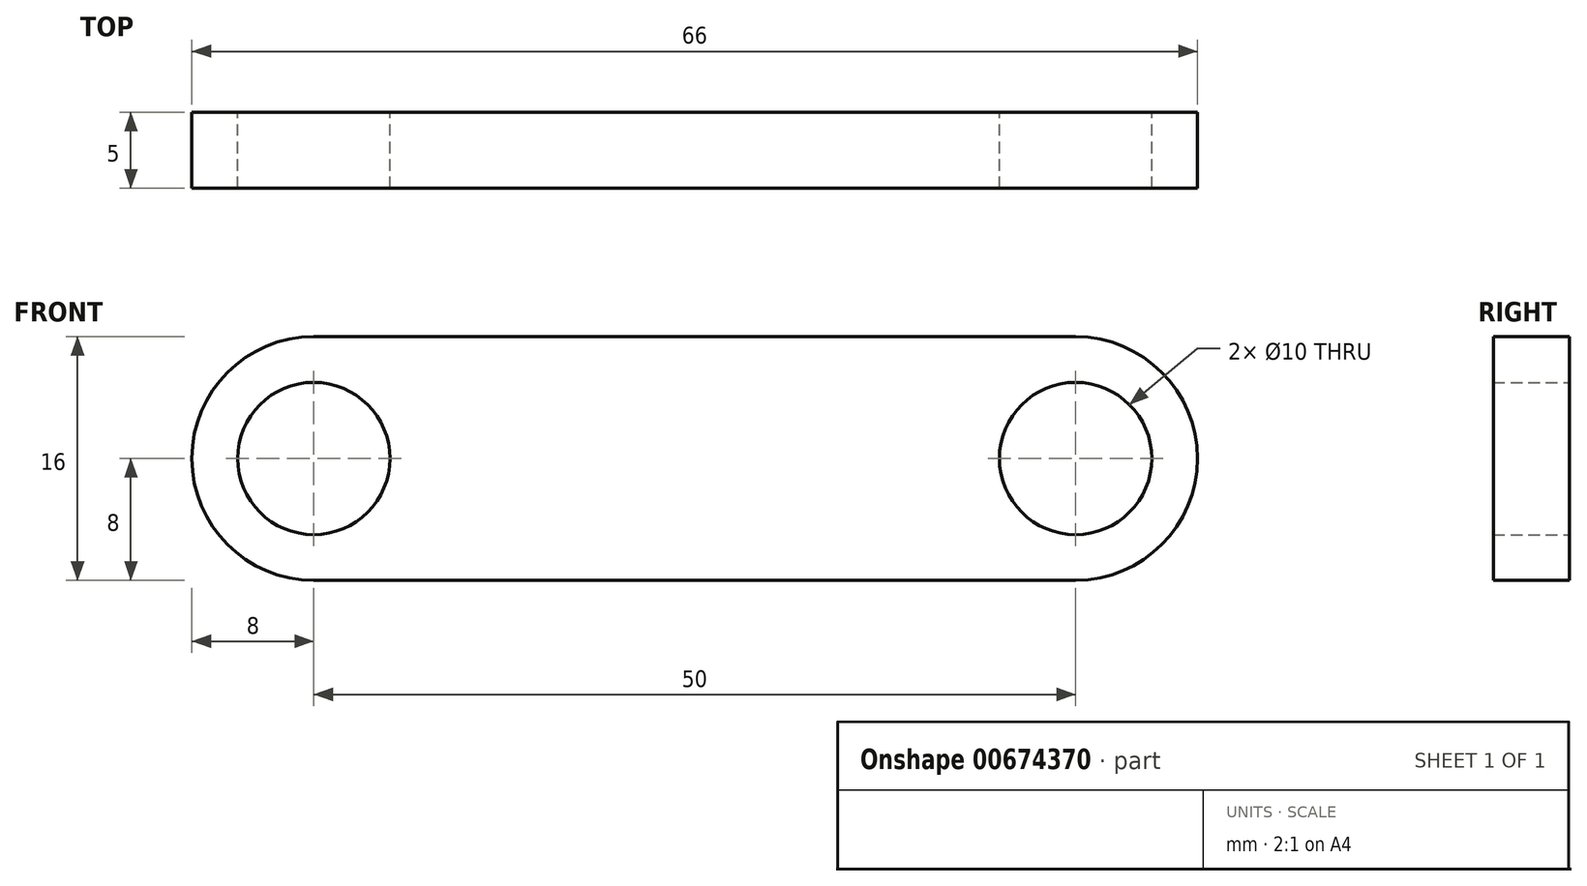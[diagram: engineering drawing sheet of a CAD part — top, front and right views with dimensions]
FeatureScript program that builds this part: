
annotation { "Feature Type Name" : "Feature", "Feature Type Description" : "" }
export const myFeature = defineFeature(function(context is Context, id is Id, definition is map)
    precondition{}
    {
        {
            var Q0;
            Q0=qCreatedBy(makeId("Front.planeOp"),FACE);
            var sketch = newSketch(context, id + "F0", { "sketchPlane" : qUnion([Q0])});
            skLineSegment(sketch, "E0.bottom", {"start": v(25, -8) * mm, "end": v(-25, -8) * mm});
            skLineSegment(sketch, "E0.top", {"start": v(25, 8) * mm, "end": v(-25, 8) * mm});
            skPoint(sketch, "E0.middle", {"position": v(0, 0) * mm});
            skArc(sketch, "E1", {"start": v(-25, 8) * mm, "mid": v(-33, 0) * mm, "end": v(-25, -8) * mm});
            skArc(sketch, "E2", {"start": v(25, -8) * mm, "mid": v(33, 0) * mm, "end": v(25, 8) * mm});
            skCircle(sketch, "E3", {"center": v(-25, 0) * mm, "radius": 5 * mm});
            skCircle(sketch, "E4", {"center": v(25, 0) * mm, "radius": 5 * mm});
            skSolve(sketch);
        }
        {
            var Q0;
            Q0 = qSketchRegion(id + "F0", true);
            extrude(context, id + "F1", {"entities" : qUnion([Q0]), "endBound" : BoundingType.SYMMETRIC, "depth" : 5 * mm, "offsetDistance" : 25.4 * mm});
        }
    });
